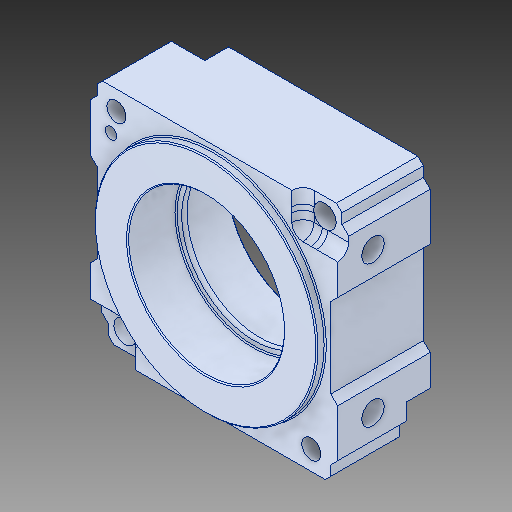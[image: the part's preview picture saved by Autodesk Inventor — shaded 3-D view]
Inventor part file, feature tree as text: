
AUTODESK INVENTOR PART (.ipt)
format: ipt  version: 2017 (Build 210142000, 142)  size: 264,704 bytes
history: native  units: in
note: dims shown in document units (in); Inventor stores cm internally (conversion verified against a paired STEP export)
features: chamfer x1
ambient origin geometry x8: Origin, YZ Plane, XZ Plane, XY Plane, X Axis, Y Axis, Z Axis, Center Point
bodies: Solid1 (feature_tree)
feature tree (1):
  chamfer  "Chamfer2"  [1 undecoded]
note: 1 required parameter value undecoded (feature->parameter linkage not recoverable at this tier; creation-order binding heuristic only, values carry confidence <= 0.55)
